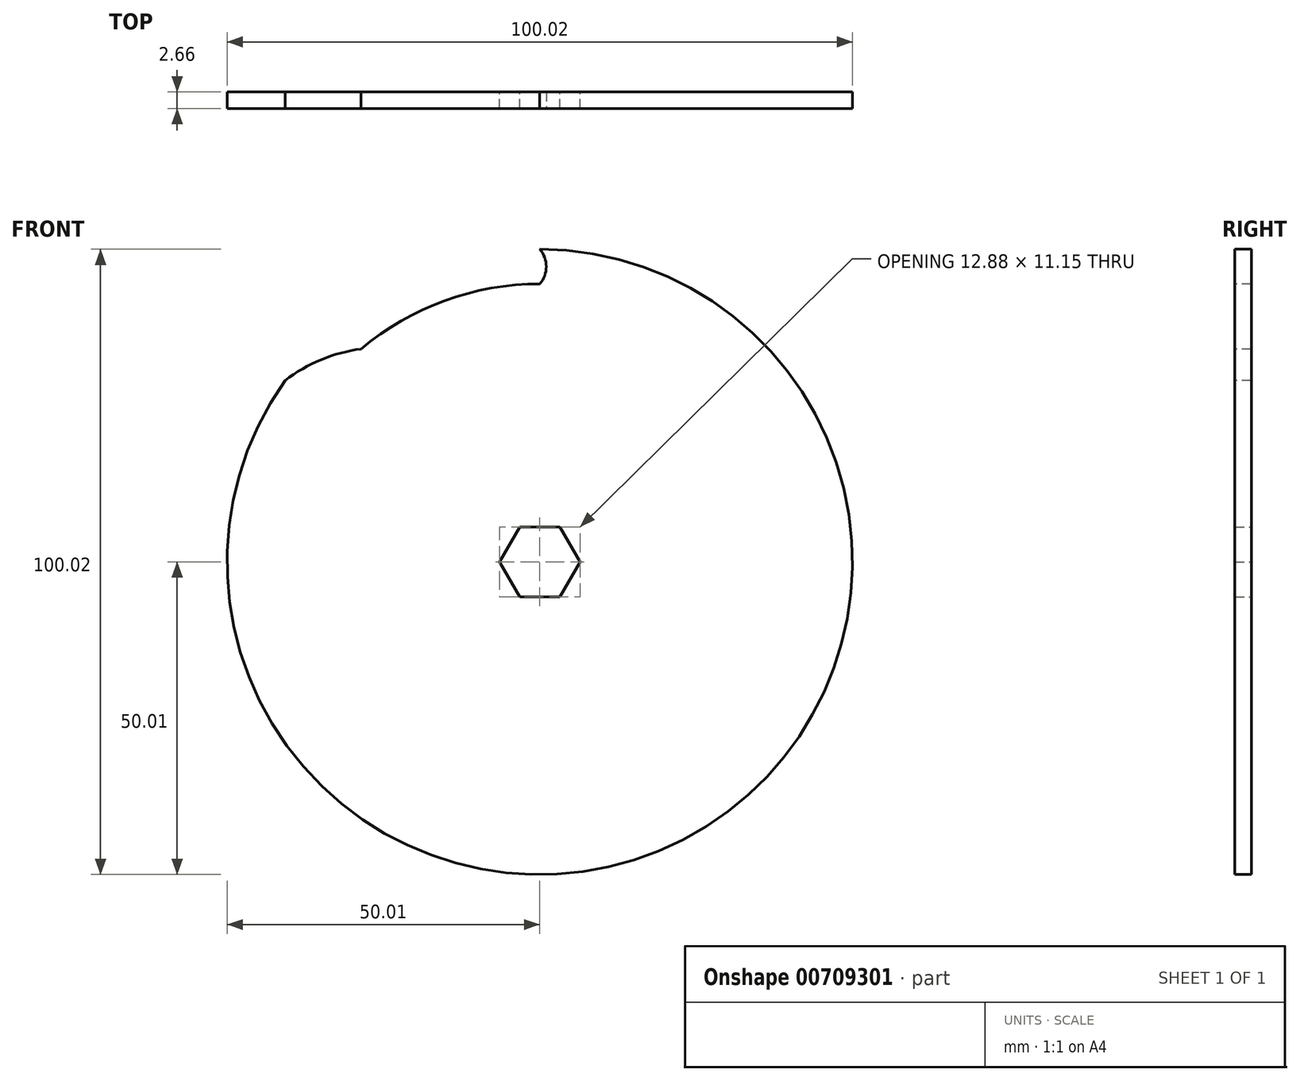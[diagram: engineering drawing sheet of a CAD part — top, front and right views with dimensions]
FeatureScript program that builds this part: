
annotation { "Feature Type Name" : "Feature", "Feature Type Description" : "" }
export const myFeature = defineFeature(function(context is Context, id is Id, definition is map)
    precondition{}
    {
        {
            var Q0;
            Q0=qCreatedBy(makeId("Front.planeOp"),FACE);
            var sketch = newSketch(context, id + "F0", { "sketchPlane" : qUnion([Q0])});
            skCircle(sketch, "E0", {"center": v(0, 0) * mm, "radius": 50 * mm});
            skCircle(sketch, "E1", {"center": v(0, 0) * mm, "radius": 44.45 * mm, "construction": true});
            skCircle(sketch, "E2", {"center": v(0, 0) * mm, "radius": 47.23 * mm, "construction": true});
            skLineSegment(sketch, "E3", {"start": v(0, 0) * mm, "end": v(0, 44.45) * mm, "construction": true});
            skLineSegment(sketch, "E4", {"start": v(0, 44.45) * mm, "end": v(0, 47.23) * mm, "construction": true});
            skLineSegment(sketch, "E5", {"start": v(0, 47.23) * mm, "end": v(0, 50) * mm, "construction": true});
            skArc(sketch, "E6", {"start": v(0, 44.45) * mm, "mid": v(1.04, 47.23) * mm, "end": v(0, 50) * mm, "construction": true});
            skCircle(sketch, "E7", {"center": v(0, 0) * mm, "radius": 6.38 * mm, "construction": true});
            skLineSegment(sketch, "E8", {"start": v(0, 0) * mm, "end": v(-38.5, 22.23) * mm, "construction": true});
            skLineSegment(sketch, "E9", {"start": v(0, 0) * mm, "end": v(-28.57, 34.05) * mm, "construction": true});
            skLineSegment(sketch, "E10", {"start": v(-38.5, 22.23) * mm, "end": v(-43.3, 25) * mm, "construction": true});
            skArc(sketch, "E11", {"start": v(-28.57, 34.05) * mm, "mid": v(-34.98, 32.33) * mm, "end": v(-40.73, 29) * mm, "construction": true});
            skCircle(sketch, "E12.cCircle", {"center": v(0, 0) * mm, "radius": 5.58 * mm, "construction": true});
            skLineSegment(sketch, "E12.0", {"start": v(-3.22, 5.58) * mm, "end": v(3.22, 5.58) * mm});
            skLineSegment(sketch, "E12.1", {"start": v(3.22, 5.58) * mm, "end": v(6.44, 0) * mm});
            skLineSegment(sketch, "E12.2", {"start": v(6.44, 0) * mm, "end": v(3.22, -5.58) * mm});
            skLineSegment(sketch, "E12.3", {"start": v(3.22, -5.58) * mm, "end": v(-3.22, -5.58) * mm});
            skLineSegment(sketch, "E12.4", {"start": v(-3.22, -5.58) * mm, "end": v(-6.44, 0) * mm});
            skLineSegment(sketch, "E12.5", {"start": v(-6.44, 0) * mm, "end": v(-3.22, 5.58) * mm});
            skPoint(sketch, "E12.0.midPoint", {"position": v(0, 5.58) * mm});
            skSolve(sketch);
        }
        {
            var Q0;
            Q0=qSketchRegion(id+"F0",true);
            extrude(context, id + "F1", {"entities" : qUnion([Q0]), "depth" : 2.67 * mm, "offsetDistance" : 25.4 * mm, "symmetric" : true});
        }
        {
            var Q0;
            Q0=qCreatedBy(makeId("Front.planeOp"),FACE);
            var sketch = newSketch(context, id + "F2", { "sketchPlane" : qUnion([Q0])});
            skArc(sketch, "E13", {"start": v(0, 44.45) * mm, "mid": v(-15.2, 41.77) * mm, "end": v(-28.57, 34.05) * mm});
            skArc(sketch, "E14", {"start": v(0, 44.45) * mm, "mid": v(1.04, 47.23) * mm, "end": v(0, 50) * mm});
            skArc(sketch, "E15", {"start": v(-28.57, 34.05) * mm, "mid": v(-34.98, 32.33) * mm, "end": v(-40.73, 29) * mm});
            skArc(sketch, "E16", {"start": v(0, 50) * mm, "mid": v(-22.91, 44.45) * mm, "end": v(-40.73, 29) * mm});
            skLineSegment(sketch, "E17", {"start": v(0, 0) * mm, "end": v(-7.72, 43.77) * mm, "construction": true});
            skSolve(sketch);
        }
        {
            var Q0;
            Q0=qSketchRegion(id+"F2",true);
            extrude(context, id + "F3", {"entities" : qUnion([Q0]), "operationType" : NewBodyOperationType.REMOVE, "oppositeDirection" : true, "depth" : 25.4 * mm, "offsetDistance" : 25.4 * mm, "hasSecondDirection" : true, "secondDirectionOppositeDirection" : false, "secondDirectionDepth" : 25.4 * mm});
        }
    });
